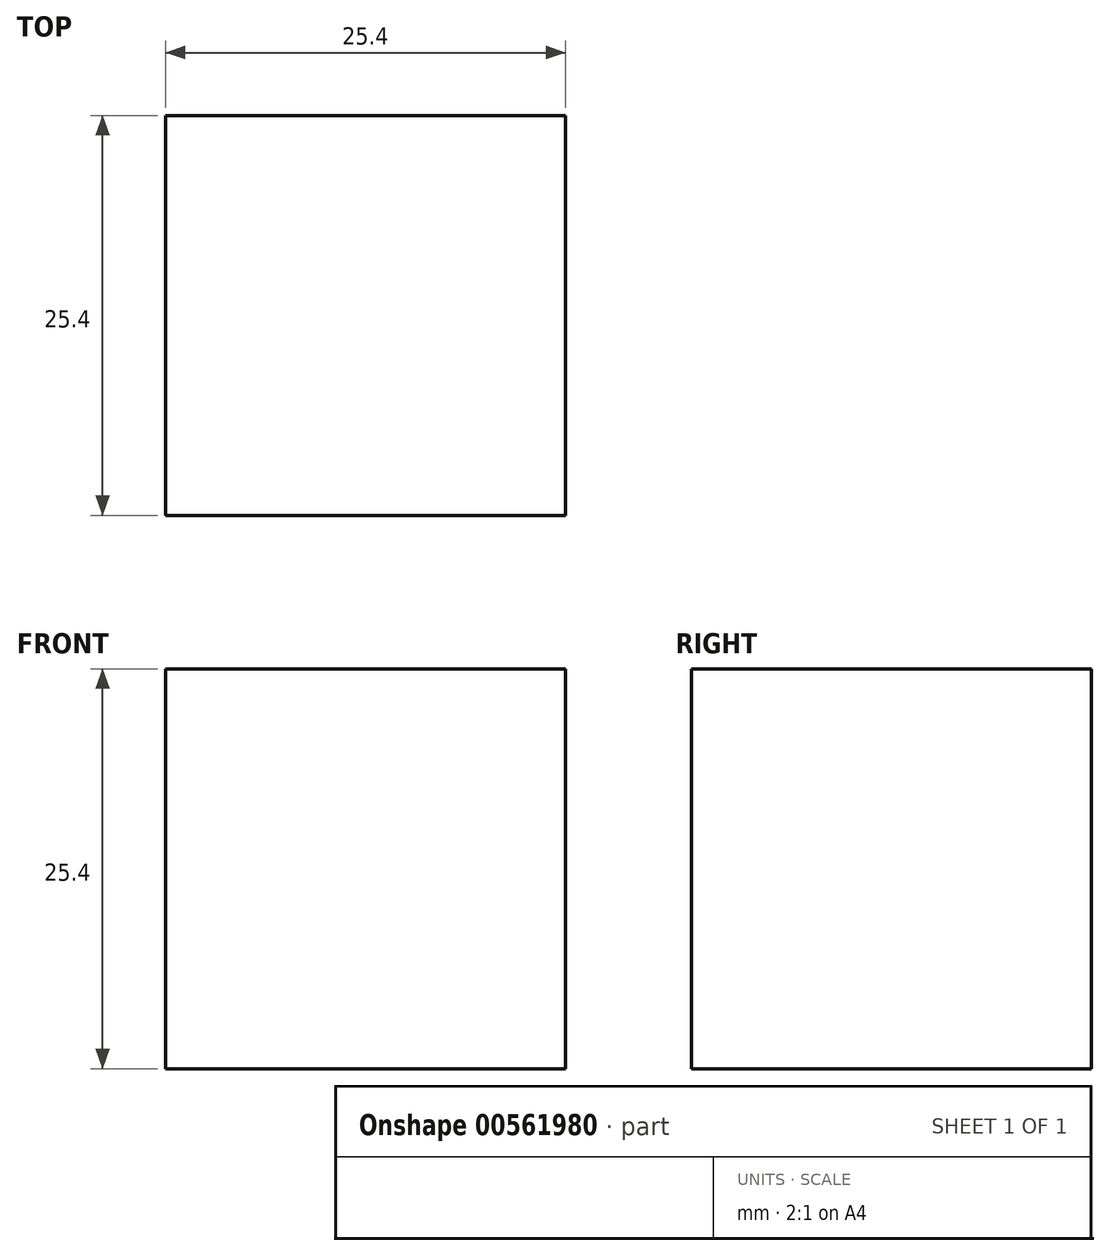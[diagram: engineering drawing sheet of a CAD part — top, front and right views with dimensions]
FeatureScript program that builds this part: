
annotation { "Feature Type Name" : "Feature", "Feature Type Description" : "" }
export const myFeature = defineFeature(function(context is Context, id is Id, definition is map)
    precondition{}
    {
        {
            var Q0;
            Q0=qCreatedBy(makeId("Front.planeOp"),FACE);
            var sketch = newSketch(context, id + "F0", { "sketchPlane" : qUnion([Q0])});
            skLineSegment(sketch, "E0.bottom", {"start": v(-27.57, 25.4) * mm, "end": v(-2.17, 25.4) * mm});
            skLineSegment(sketch, "E0.top", {"start": v(-27.57, 0) * mm, "end": v(-2.17, 0) * mm});
            skLineSegment(sketch, "E0.left", {"start": v(-27.57, 25.4) * mm, "end": v(-27.57, 0) * mm});
            skLineSegment(sketch, "E0.right", {"start": v(-2.17, 25.4) * mm, "end": v(-2.17, 0) * mm});
            skSolve(sketch);
        }
        {
            var Q0;
            Q0=makeQuery(id+"F0.imprint","IMPRINT",FACE,{"disambiguationData":[TD([[makeQuery(id+"F0.imprint","IMPRINT",EDGE,{"derivedFrom":sQuery(id+"F0.wireOp",EDGE,"E0.bottom")}),-1.0]])]});
            extrude(context, id + "F1", {"entities" : qUnion([Q0]), "depth" : 25.4 * mm, "offsetDistance" : 25.4 * mm});
        }
    });
